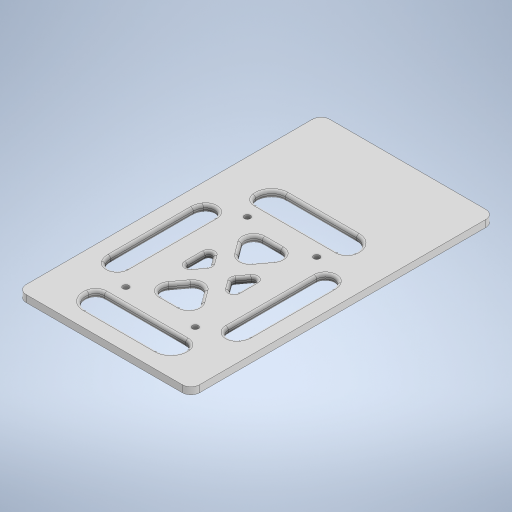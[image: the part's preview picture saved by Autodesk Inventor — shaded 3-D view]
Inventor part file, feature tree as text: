
AUTODESK INVENTOR PART (.ipt)
format: ipt  version: 2023 (Build 270158000, 158)  size: 557,056 bytes
history: native  units: in
note: dims shown in document units (in); Inventor stores cm internally (conversion verified against a paired STEP export)
features: fillet x6, sketch x3, extrude x2, hole x1, thicken_offset x1
ambient origin geometry x8: Origin, YZ Plane, XZ Plane, XY Plane, X Axis, Y Axis, Z Axis, Center Point
bodies: Solid1 (feature_tree)
feature tree (13):
  extrude  "Extrusion1"  Depth=3.937in
  hole  "Hole1"  [1 undecoded]
  extrude  "Extrusion3"  Depth=0.3937in
  thicken_offset  "Thicken1"
  fillet  "Fillet4"  Radius=0.1969in
  fillet  "Fillet5"  Radius=0.3937in
  fillet  "Fillet6"  Radius=0.1969in
  fillet  "Fillet7"  Radius=0.1969in
  fillet  "Fillet8"  Radius=0.1969in
  fillet  "Fillet9"  Radius=0.1969in
  sketch  "Sketch1"  dims[d0=5.315in d1=3.937in]
  sketch  "Sketch3"  dims[d2=0.1575in d3=0.0in d11=1.9685in]
  sketch  "Sketch4"  dims[d12=3.1496in d18=0.1339in d19=0.2362in d20=0.248in d21=0.0787in d22=90.0deg d23=0.315in d24=0.8108in d27=0.3937in d28=0.1969in d29=0.3937in d30=0.1969in d31=0.1969in d32=0.1969in d33=0.1969in d34=0.0in d35=0.0in d37=1.9291in d38=3.0709in d40=1.5748in d41=1.1811in d42=0.1969in d43=0.315in d44=0.1969in d45=0.0787in d46=0.1969in d47=0.0591in d48=0.1969in]
note: 1 required parameter value undecoded (feature->parameter linkage not recoverable at this tier; creation-order binding heuristic only, values carry confidence <= 0.55)
